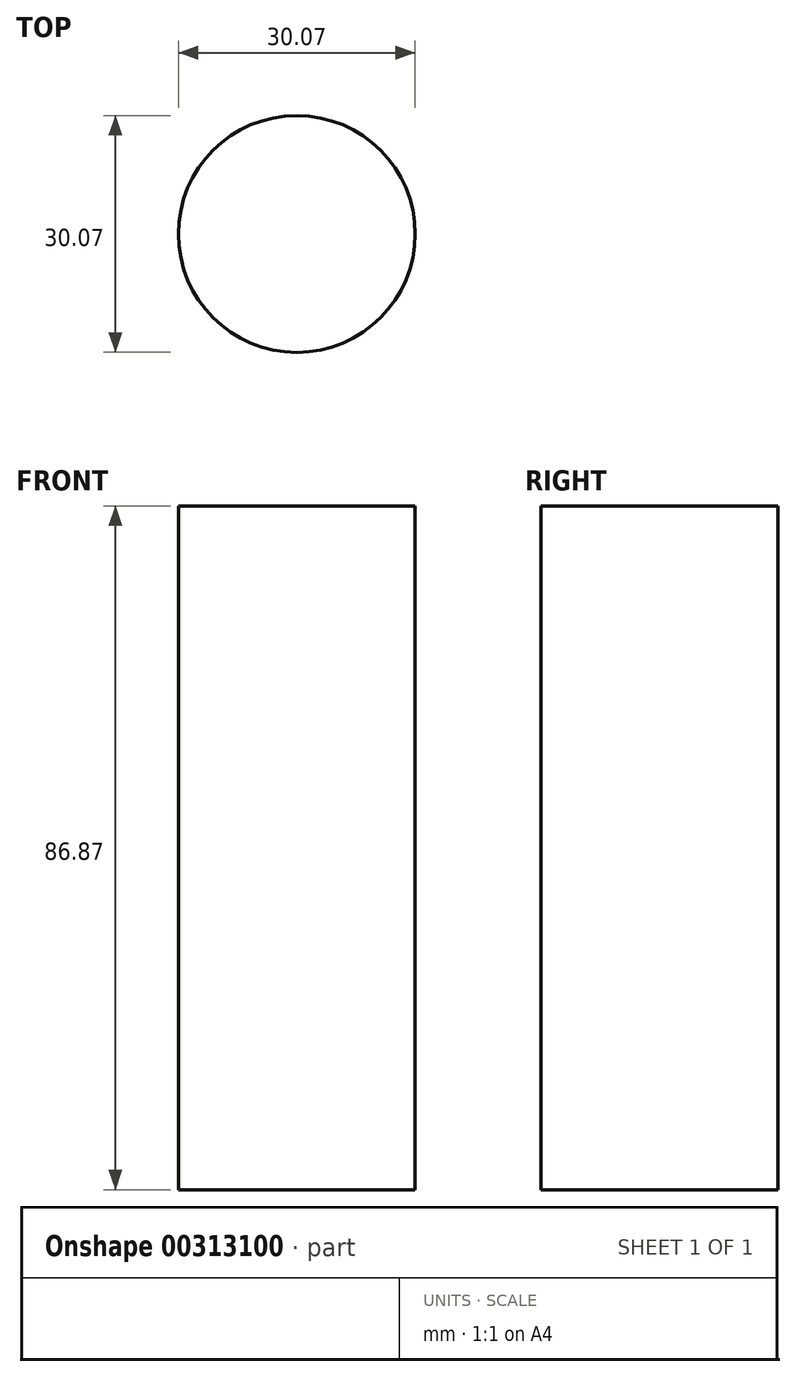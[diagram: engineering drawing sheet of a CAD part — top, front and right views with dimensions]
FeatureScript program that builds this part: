
annotation { "Feature Type Name" : "Feature", "Feature Type Description" : "" }
export const myFeature = defineFeature(function(context is Context, id is Id, definition is map)
    precondition{}
    {
        {
            var Q0;
            Q0=qCreatedBy(makeId("Top.planeOp"),FACE);
            var sketch = newSketch(context, id + "F0", { "sketchPlane" : qUnion([Q0])});
            skCircle(sketch, "E0", {"center": v(-59.67, -24.9) * mm, "radius": 15.04 * mm});
            skSolve(sketch);
        }
        {
            var Q0;
            Q0 = qSketchRegion(id + "F0", true);
            extrude(context, id + "F1", {"entities" : qUnion([Q0]), "depth" : 86.87 * mm});
        }
    });
